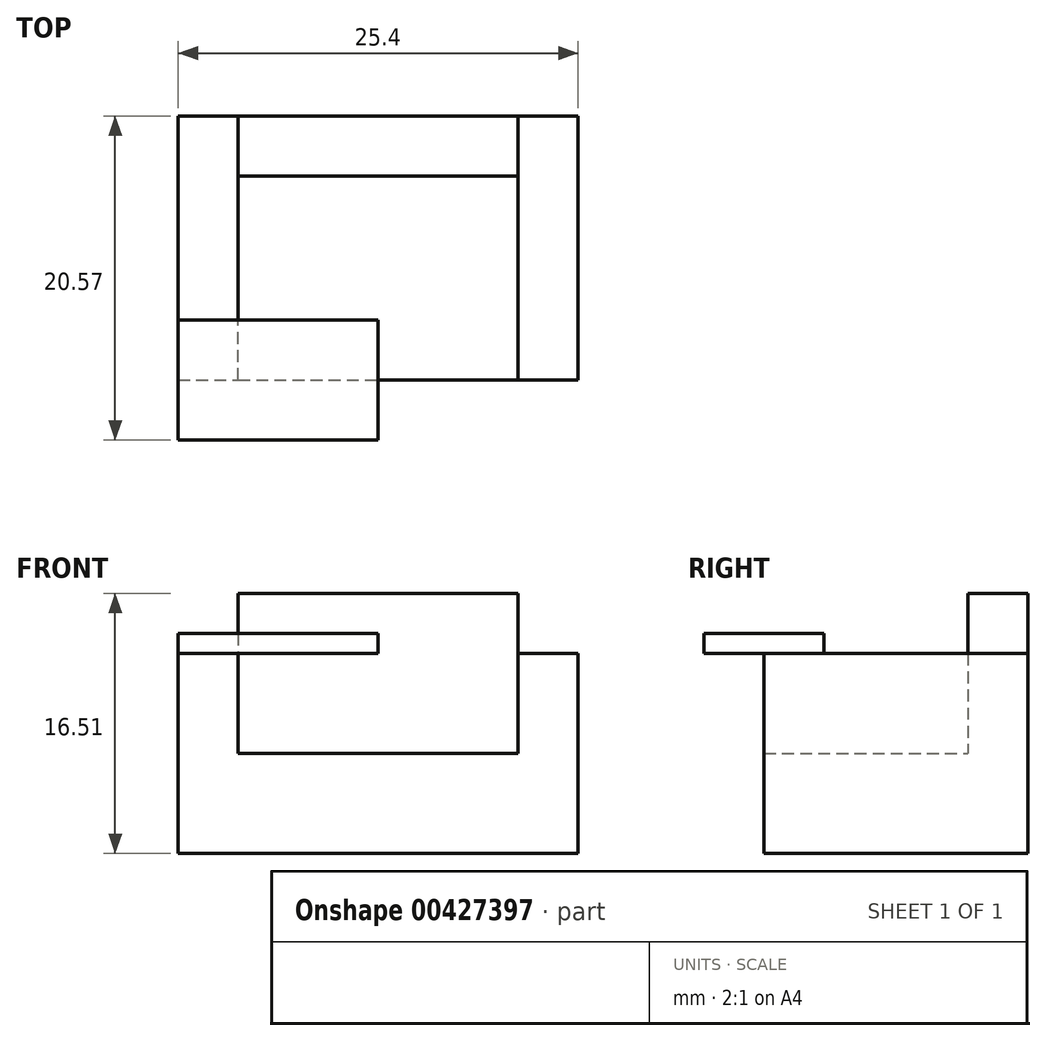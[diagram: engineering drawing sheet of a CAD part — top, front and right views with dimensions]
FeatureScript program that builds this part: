
annotation { "Feature Type Name" : "Feature", "Feature Type Description" : "" }
export const myFeature = defineFeature(function(context is Context, id is Id, definition is map)
    precondition{}
    {
        {
            var Q0;
            Q0=qCreatedBy(makeId("Front.planeOp"),FACE);
            var sketch = newSketch(context, id + "F0", { "sketchPlane" : qUnion([Q0])});
            skLineSegment(sketch, "E0", {"start": v(0, -6.35) * mm, "end": v(-12.7, -6.35) * mm});
            skLineSegment(sketch, "E1", {"start": v(-12.7, -6.35) * mm, "end": v(-12.7, 0) * mm});
            skLineSegment(sketch, "E2.MirrorCS", {"start": v(0, -6.35) * mm, "end": v(12.7, -6.35) * mm});
            skLineSegment(sketch, "E3.MirrorCS", {"start": v(12.7, -6.35) * mm, "end": v(12.7, 0) * mm});
            skLineSegment(sketch, "E4", {"start": v(-12.7, 0) * mm, "end": v(12.7, 0) * mm});
            skSolve(sketch);
        }
        {
            var Q0;
            Q0 = qSketchRegion(id + "F0", true);
            extrude(context, id + "F1", {"entities" : qUnion([Q0]), "depth" : 16.76 * mm});
        }
        {
            var Q0;
            Q0=makeQuery(id+"F1.opExtrude","SWEPT_FACE",FACE,{"disambiguationData":[OSD([sQuery(id+"F0.wireOp",EDGE,"E4")])]});
            var sketch = newSketch(context, id + "F2", { "sketchPlane" : qUnion([Q0])});
            skLineSegment(sketch, "E5", {"start": v(-12.7, -16.76) * mm, "end": v(-8.89, -16.76) * mm});
            skLineSegment(sketch, "E6", {"start": v(-8.89, -16.76) * mm, "end": v(-8.89, -3.81) * mm});
            skLineSegment(sketch, "E7", {"start": v(-8.89, -3.81) * mm, "end": v(0, -3.81) * mm});
            skLineSegment(sketch, "E8.MirrorCS", {"start": v(8.89, -3.81) * mm, "end": v(0, -3.81) * mm});
            skLineSegment(sketch, "E9.MirrorCS", {"start": v(8.89, -16.76) * mm, "end": v(8.89, -3.81) * mm});
            skLineSegment(sketch, "E10.MirrorCS", {"start": v(12.7, -16.76) * mm, "end": v(8.89, -16.76) * mm});
            skLineSegment(sketch, "E11", {"start": v(-12.7, -16.76) * mm, "end": v(-12.7, 0) * mm});
            skLineSegment(sketch, "E12", {"start": v(-12.7, 0) * mm, "end": v(12.7, 0) * mm});
            skLineSegment(sketch, "E13", {"start": v(12.7, 0) * mm, "end": v(12.7, -16.76) * mm});
            skSolve(sketch);
        }
        {
            var Q0;
            Q0 = qSketchRegion(id + "F2", true);
            extrude(context, id + "F3", {"entities" : qUnion([Q0]), "operationType" : NewBodyOperationType.ADD, "depth" : 6.35 * mm});
        }
        {
            var Q0;
            Q0=makeQuery(id+"F3.opExtrude","CAP_FACE",FACE,{"disambiguationData":[OSD([sQuery(id+"F2.wireOp",EDGE,"E5"),sQuery(id+"F2.wireOp",EDGE,"E6"),sQuery(id+"F2.wireOp",EDGE,"E7"),sQuery(id+"F2.wireOp",EDGE,"E8.MirrorCS"),sQuery(id+"F2.wireOp",EDGE,"E9.MirrorCS"),sQuery(id+"F2.wireOp",EDGE,"E10.MirrorCS"),sQuery(id+"F2.wireOp",EDGE,"E11"),sQuery(id+"F2.wireOp",EDGE,"E12"),sQuery(id+"F2.wireOp",EDGE,"E13")])],"isStart":false});
            var sketch = newSketch(context, id + "F4", { "sketchPlane" : qUnion([Q0])});
            skLineSegment(sketch, "E14", {"start": v(-8.89, -3.81) * mm, "end": v(-8.89, 0) * mm});
            skLineSegment(sketch, "E15", {"start": v(8.89, -3.81) * mm, "end": v(8.89, 0) * mm});
            skLineSegment(sketch, "E16", {"start": v(8.89, 0) * mm, "end": v(-8.89, 0) * mm});
            skLineSegment(sketch, "E17", {"start": v(-8.89, -3.81) * mm, "end": v(8.89, -3.81) * mm});
            skSolve(sketch);
        }
        {
            var Q0;
            Q0 = qSketchRegion(id + "F4", true);
            extrude(context, id + "F5", {"entities" : qUnion([Q0]), "operationType" : NewBodyOperationType.ADD, "depth" : 3.8 * mm});
        }
        {
            var Q0;
            {var subQ0=sQuery(id+"F2.wireOp",EDGE,"E12");var subQ1=sQuery(id+"F2.wireOp",EDGE,"E11");var subQ2=sQuery(id+"F2.wireOp",EDGE,"E10.MirrorCS");var subQ3=sQuery(id+"F2.wireOp",EDGE,"E8.MirrorCS");var subQ4=sQuery(id+"F2.wireOp",EDGE,"E7");var subQ5=sQuery(id+"F2.wireOp",EDGE,"E6");var subQ9=sQuery(id+"F0.wireOp",EDGE,"E1");var subQ11=sQuery(id+"F2.wireOp",EDGE,"E5");Q0=makeQuery(id+"F5.boolean.opBoolean","SPLIT",FACE,{"disambiguationData":[TD([makeQuery(id+"F1.opExtrude","SWEPT_FACE",FACE,{"disambiguationData":[OSD([subQ9])]})])],"derivedFrom":makeQuery(id+"F3.opExtrude","CAP_FACE",FACE,{"disambiguationData":[OSD([subQ11,subQ5,subQ4,subQ3,sQuery(id+"F2.wireOp",EDGE,"E9.MirrorCS"),subQ2,subQ1,subQ0,sQuery(id+"F2.wireOp",EDGE,"E13")])],"isStart":false})});}
            var sketch = newSketch(context, id + "F6", { "sketchPlane" : qUnion([Q0])});
            skLineSegment(sketch, "E18", {"start": v(-12.7, -16.76) * mm, "end": v(-12.7, -12.95) * mm});
            skLineSegment(sketch, "E19", {"start": v(-12.7, -16.76) * mm, "end": v(-12.7, -20.57) * mm});
            skLineSegment(sketch, "E20", {"start": v(-12.7, -12.95) * mm, "end": v(0, -12.95) * mm});
            skLineSegment(sketch, "E21", {"start": v(-12.7, -20.57) * mm, "end": v(0, -20.57) * mm});
            skLineSegment(sketch, "E22", {"start": v(0, -20.57) * mm, "end": v(0, -12.95) * mm});
            skSolve(sketch);
        }
        {
            var Q0;
            Q0 = qSketchRegion(id + "F6", true);
            extrude(context, id + "F7", {"entities" : qUnion([Q0]), "operationType" : NewBodyOperationType.ADD, "depth" : 1.27 * mm});
        }
    });
